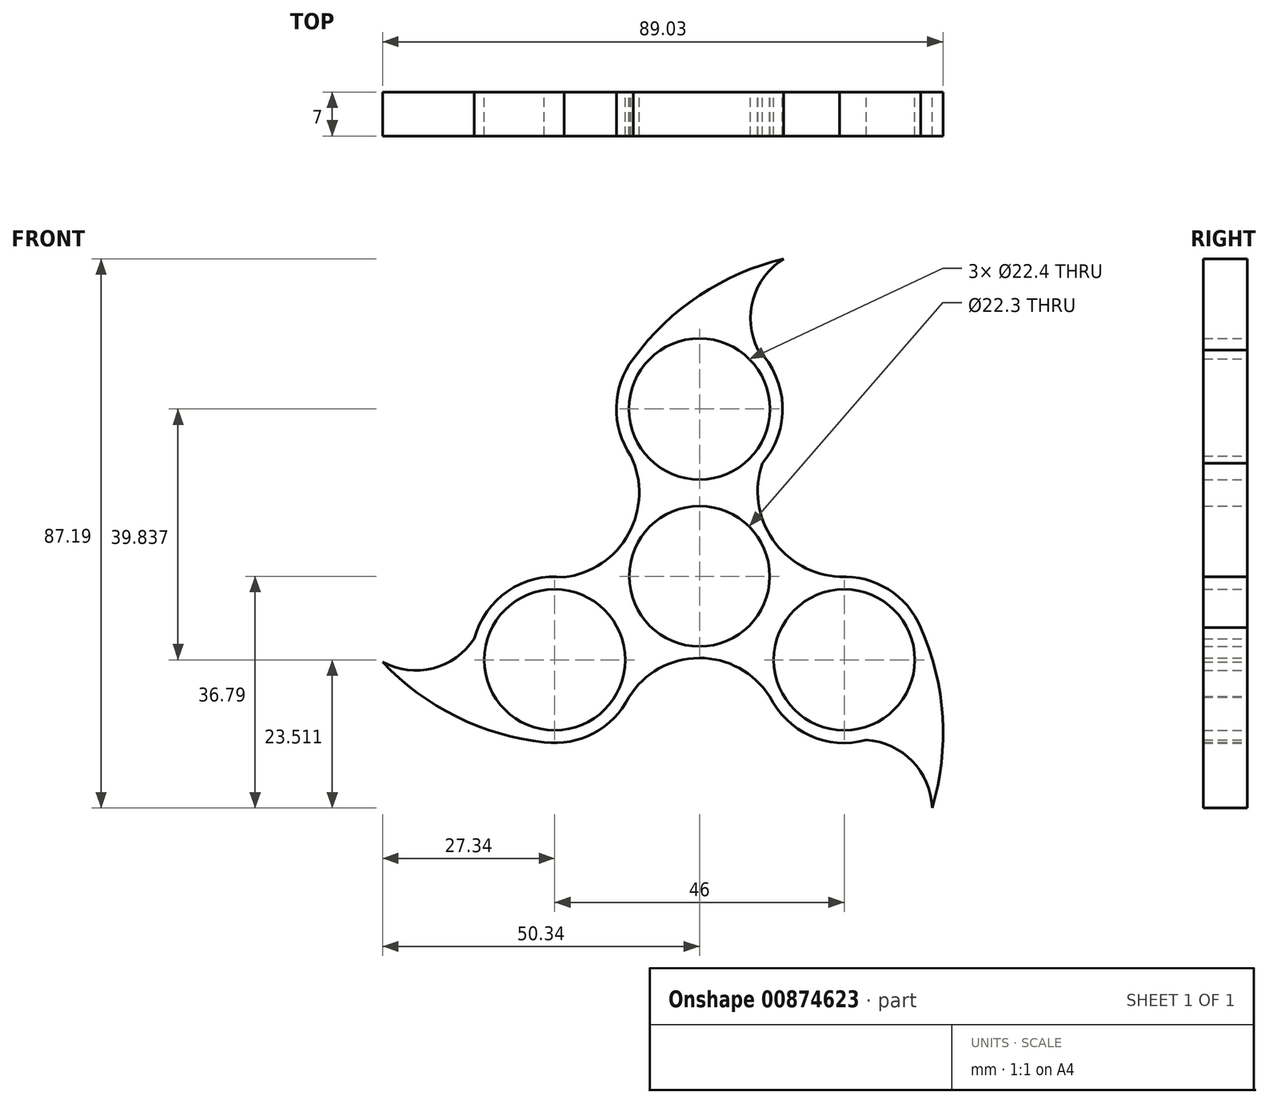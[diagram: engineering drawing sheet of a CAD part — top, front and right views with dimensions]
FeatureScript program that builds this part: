
annotation { "Feature Type Name" : "Feature", "Feature Type Description" : "" }
export const myFeature = defineFeature(function(context is Context, id is Id, definition is map)
    precondition{}
    {
        {
            var Q0;
            Q0=qCreatedBy(makeId("Front.planeOp"),FACE);
            var sketch = newSketch(context, id + "F0", { "sketchPlane" : qUnion([Q0])});
            skCircle(sketch, "E0", {"center": v(0, 0) * mm, "radius": 11.15 * mm});
            skCircle(sketch, "E1", {"center": v(0, 26.56) * mm, "radius": 11.2 * mm});
            skArc(sketch, "E2", {"start": v(9.97, 17.91) * mm, "mid": v(13.2, 27.06) * mm, "end": v(9.29, 35.94) * mm});
            skCircle(sketch, "E3.1.0", {"center": v(-23, -13.28) * mm, "radius": 11.2 * mm});
            skArc(sketch, "E3.1.1", {"start": v(-24.65, -26.38) * mm, "mid": v(-16.78, -24.92) * mm, "end": v(-11.2, -19.19) * mm});
            skCircle(sketch, "E3.2.0", {"center": v(23, -13.28) * mm, "radius": 11.2 * mm});
            skArc(sketch, "E3.2.1", {"start": v(11.14, -19.07) * mm, "mid": v(17.56, -25.3) * mm, "end": v(26.48, -26.01) * mm});
            skArc(sketch, "E4", {"start": v(12.53, 22.4) * mm, "mid": v(10.38, 8.1) * mm, "end": v(22.28, -0.1) * mm});
            skArc(sketch, "E5", {"start": v(-21.5, -0.16) * mm, "mid": v(-10.78, 7.68) * mm, "end": v(-11.93, 20.92) * mm});
            skArc(sketch, "E6", {"start": v(11.14, -19.07) * mm, "mid": v(-0.7, -13) * mm, "end": v(-11.82, -20.3) * mm});
            skArc(sketch, "E7", {"start": v(-50.34, -13.6) * mm, "mid": v(-38.63, -22.28) * mm, "end": v(-24.65, -26.38) * mm});
            skArc(sketch, "E8", {"start": v(-50.34, -13.6) * mm, "mid": v(-40.5, -13.96) * mm, "end": v(-34.24, -6.35) * mm});
            skArc(sketch, "E9.1.0", {"start": v(36.96, -36.8) * mm, "mid": v(38.61, -22.32) * mm, "end": v(35.17, -8.16) * mm});
            skArc(sketch, "E9.1.1", {"start": v(36.96, -36.8) * mm, "mid": v(32.34, -28.09) * mm, "end": v(22.62, -26.47) * mm});
            skArc(sketch, "E9.2.0", {"start": v(13.38, 50.4) * mm, "mid": v(0.02, 44.6) * mm, "end": v(-10.52, 34.54) * mm});
            skArc(sketch, "E9.2.1", {"start": v(13.38, 50.4) * mm, "mid": v(8.15, 42.05) * mm, "end": v(11.62, 32.83) * mm});
            skArc(sketch, "E10.trimOffspring", {"start": v(-21.5, -0.16) * mm, "mid": v(-30.46, -2.39) * mm, "end": v(-35.77, -9.93) * mm});
            skArc(sketch, "E11.trimOffspring", {"start": v(35.17, -8.16) * mm, "mid": v(30, -2.09) * mm, "end": v(22.28, -0.1) * mm});
            skArc(sketch, "E12.trimOffspring", {"start": v(-10.52, 34.54) * mm, "mid": v(-13.2, 26.87) * mm, "end": v(-10.88, 19.09) * mm});
            skSolve(sketch);
        }
        {
            var Q0;
            Q0 = qSketchRegion(id + "F0", true);
            extrude(context, id + "F1", {"entities" : qUnion([Q0]), "depth" : 7 * mm, "offsetDistance" : 25 * mm});
        }
    });
